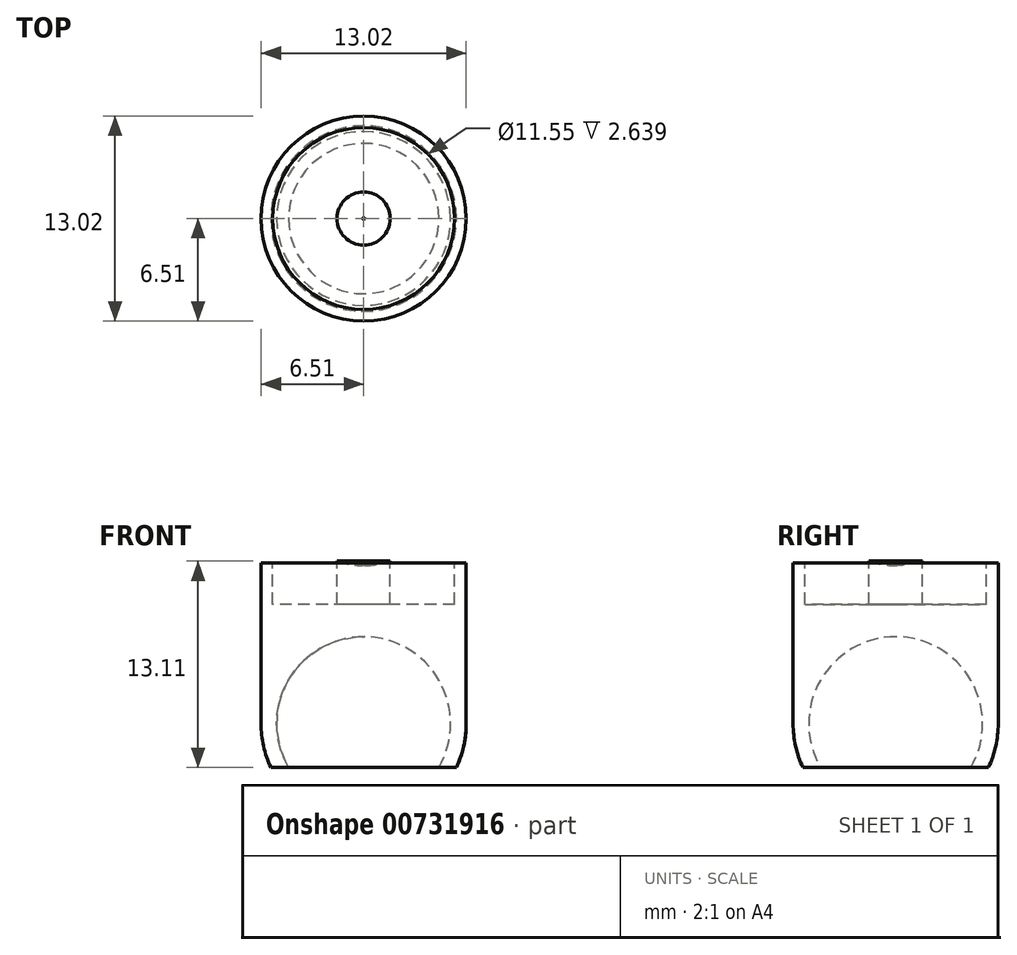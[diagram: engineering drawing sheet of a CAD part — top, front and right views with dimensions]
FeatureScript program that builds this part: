
annotation { "Feature Type Name" : "Feature", "Feature Type Description" : "" }
export const myFeature = defineFeature(function(context is Context, id is Id, definition is map)
    precondition{}
    {
        {
            var Q0;
            Q0=qCreatedBy(makeId("Front.planeOp"),FACE);
            var sketch = newSketch(context, id + "F0", { "sketchPlane" : qUnion([Q0])});
            skLineSegment(sketch, "E0.bottom", {"start": v(-6.51, 0) * mm, "end": v(6.51, 0) * mm});
            skLineSegment(sketch, "E1", {"start": v(-7.06, -2.78) * mm, "end": v(9.45, -2.78) * mm, "construction": true});
            skLineSegment(sketch, "E2", {"start": v(-5.9, -2.78) * mm, "end": v(-4.77, -2.78) * mm});
            skLineSegment(sketch, "E3", {"start": v(4.77, -2.78) * mm, "end": v(5.9, -2.78) * mm});
            skArc(sketch, "E4", {"start": v(0, 20.05) * mm, "mid": v(-5.03, 15.05) * mm, "end": v(0, 10.05) * mm});
            skLineSegment(sketch, "E5", {"start": v(-5.77, 7.58) * mm, "end": v(-1.69, 7.58) * mm});
            skLineSegment(sketch, "E6", {"start": v(-1.69, 7.58) * mm, "end": v(-1.69, 10.33) * mm});
            skLineSegment(sketch, "E7", {"start": v(0, 21.68) * mm, "end": v(0, -6) * mm, "construction": true});
            skPoint(sketch, "E0.right.end.orphan", {"position": v(6.51, 15.06) * mm});
            skArc(sketch, "E8.trimOffspring", {"start": v(-6.51, 0) * mm, "mid": v(-6.36, -1.42) * mm, "end": v(-5.9, -2.78) * mm});
            skArc(sketch, "E9.trimOffspring", {"start": v(0, 5.52) * mm, "mid": v(-4.79, 2.75) * mm, "end": v(-4.77, -2.78) * mm});
            skLineSegment(sketch, "E10", {"start": v(0, 10.05) * mm, "end": v(0, 5.52) * mm});
            skLineSegment(sketch, "E11", {"start": v(0, 20.05) * mm, "end": v(0, 10.05) * mm});
            skLineSegment(sketch, "E12", {"start": v(-5.77, 10.21) * mm, "end": v(-5.77, 7.58) * mm});
            skLineSegment(sketch, "E13", {"start": v(-6.51, 0) * mm, "end": v(-6.51, 10.21) * mm});
            skLineSegment(sketch, "E14", {"start": v(-4.77, -2.78) * mm, "end": v(-4.77, 22.6) * mm, "construction": true});
            skLineSegment(sketch, "E15", {"start": v(-5.77, 10.21) * mm, "end": v(-6.51, 10.21) * mm});
            skSolve(sketch);
        }
        {
            var Q0;
            {var subQ0=sQuery(id+"F0.wireOp",EDGE,"E11");Q0=makeQuery(id+"F0.imprint","IMPRINT",FACE,{"disambiguationData":[TD([[makeQuery(id+"F0.imprint","IMPRINT",EDGE,{"derivedFrom":subQ0}),-1.0]])]});}
            var Q1;
            Q1=makeQuery(id+"F0.imprint","IMPRINT",FACE,{"disambiguationData":[TD([[makeQuery(id+"F0.imprint","IMPRINT",EDGE,{"derivedFrom":sQuery(id+"F0.wireOp",EDGE,"E5")}),-1.0]])]});
            var Q2;
            {var subQ4=sQuery(id+"F0.wireOp",EDGE,"E2");Q2=makeQuery(id+"F0.imprint","IMPRINT",FACE,{"disambiguationData":[TD([[makeQuery(id+"F0.imprint","IMPRINT",EDGE,{"derivedFrom":subQ4}),1.0]])]});}
            var Q3;
            Q3=sQuery(id+"F0.wireOp",EDGE,"E7");
            revolve(context, id + "F1", {"surfaceOperationType" : NewSurfaceOperationType.NEW, "entities" : qUnion([Q0, Q1, Q2]), "axis" : qUnion([Q3]), "revolveType" : RevolveType.FULL});
        }
    });
